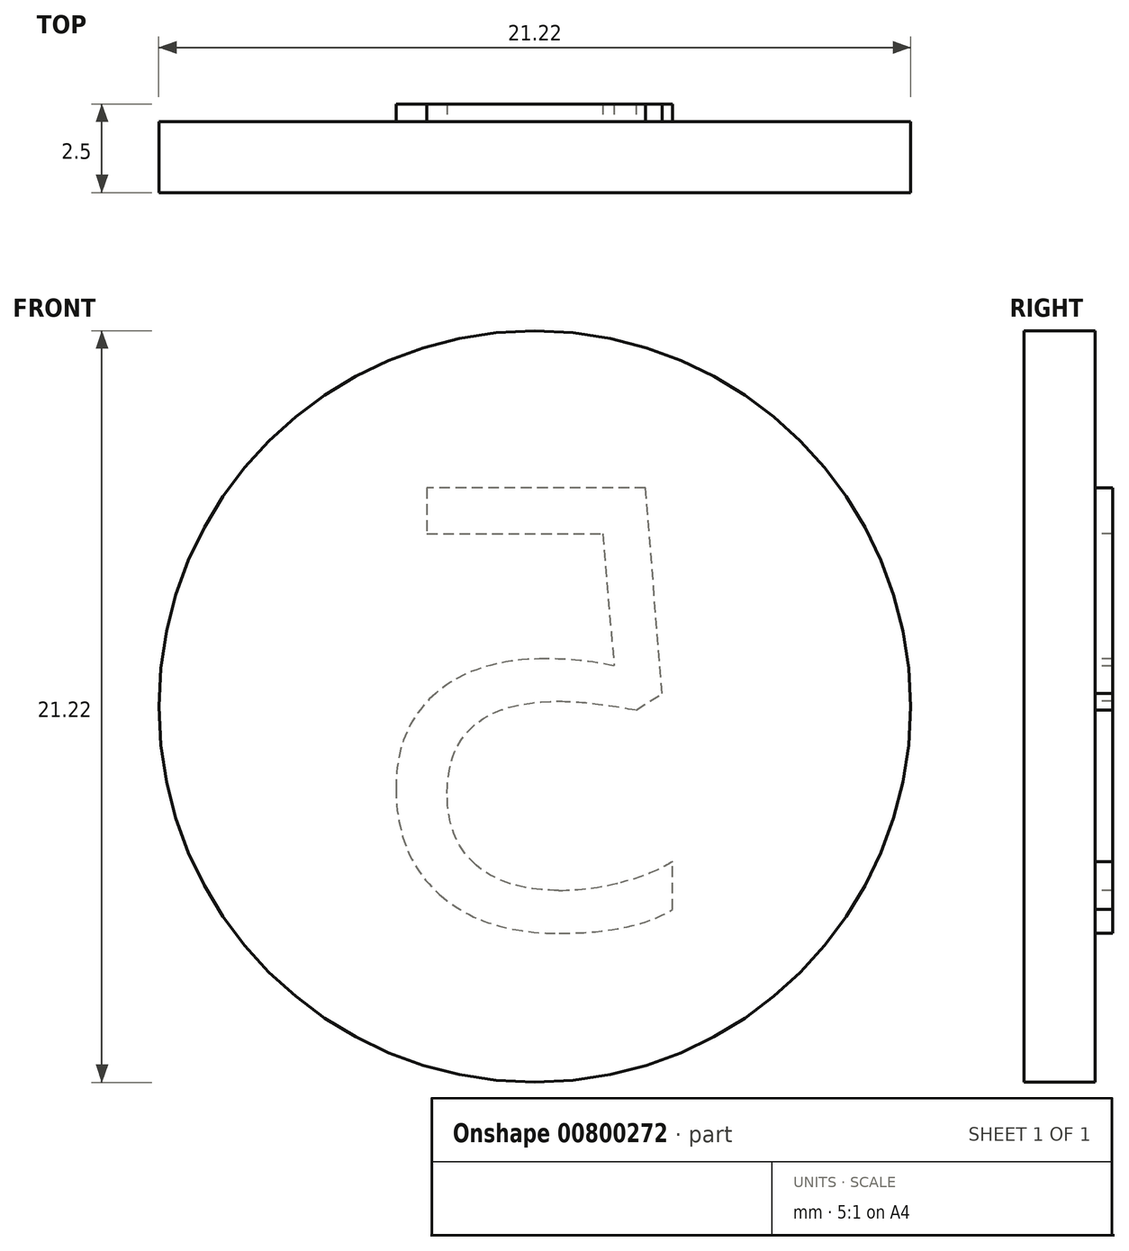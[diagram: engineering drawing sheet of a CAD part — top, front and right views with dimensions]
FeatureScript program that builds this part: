
annotation { "Feature Type Name" : "Feature", "Feature Type Description" : "" }
export const myFeature = defineFeature(function(context is Context, id is Id, definition is map)
    precondition{}
    {
        {
            var Q0;
            Q0=qCreatedBy(makeId("Front.planeOp"),FACE);
            var sketch = newSketch(context, id + "F0", { "sketchPlane" : qUnion([Q0])});
            skCircle(sketch, "E0", {"center": v(0, 0) * mm, "radius": 10.6 * mm});
            skSolve(sketch);
        }
        {
            var Q0;
            Q0=makeQuery(id+"F0.imprint","IMPRINT",FACE,{"disambiguationData":[TD([[makeQuery(id+"F0.imprint","IMPRINT",EDGE,{"derivedFrom":sQuery(id+"F0.wireOp",EDGE,"E0")}),1.0]])]});
            extrude(context, id + "F1", {"entities" : qUnion([Q0]), "depth" : 2 * mm, "offsetDistance" : 25 * mm});
        }
        {
            var Q0;
            Q0=makeQuery(id+"F1.opExtrude","CAP_FACE",FACE,{"disambiguationData":[OSD([sQuery(id+"F0.wireOp",EDGE,"E0")])],"isStart":true});
            var sketch = newSketch(context, id + "F2", { "sketchPlane" : qUnion([Q0])});
            skText(sketch, "E1", { "text": "5", "fontName": "OpenSans-Regular.ttf"});
            const initialGuessF2  = {"E1": [-0.00502, -0.00623, 1, 0, 0.01251]};
            skSetInitialGuess(sketch, initialGuessF2);
            skSolve(sketch);
        }
        {
            var Q0;
            Q0=makeQuery(id+"F2.imprint","IMPRINT",FACE,{"disambiguationData":[TD([[makeQuery(id+"F2.imprint","IMPRINT",EDGE,{"derivedFrom":sQuery(id+"F2.wireOp",EDGE,"E1.sketch_text.stroke-0")}),-1.0]])]});
            extrude(context, id + "F3", {"entities" : qUnion([Q0]), "operationType" : NewBodyOperationType.ADD, "depth" : .5 * mm, "offsetDistance" : 25 * mm});
        }
    });
